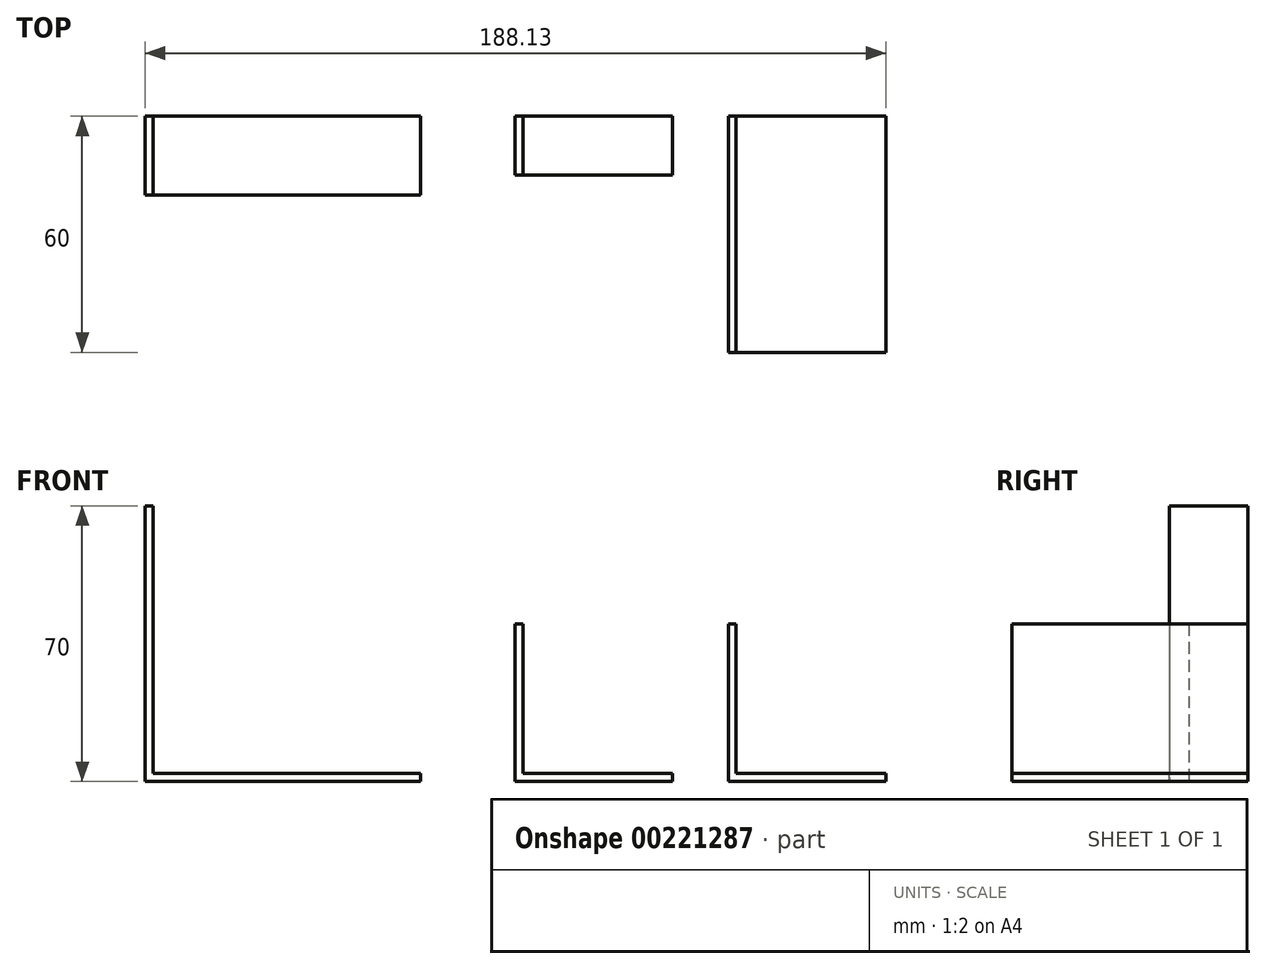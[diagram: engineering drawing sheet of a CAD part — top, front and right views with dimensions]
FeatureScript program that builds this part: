
annotation { "Feature Type Name" : "Feature", "Feature Type Description" : "" }
export const myFeature = defineFeature(function(context is Context, id is Id, definition is map)
    precondition{}
    {
        {
            var Q0;
            Q0=qCreatedBy(makeId("Front.planeOp"),FACE);
            var sketch = newSketch(context, id + "F0", { "sketchPlane" : qUnion([Q0])});
            skLineSegment(sketch, "E0.bottom", {"start": v(-61.82, 70) * mm, "end": v(-59.82, 70) * mm});
            skLineSegment(sketch, "E0.top", {"start": v(-61.82, 0) * mm, "end": v(-59.82, 0) * mm});
            skLineSegment(sketch, "E0.left", {"start": v(-61.82, 70) * mm, "end": v(-61.82, 0) * mm});
            skLineSegment(sketch, "E0.right", {"start": v(-59.82, 70) * mm, "end": v(-59.82, 2) * mm});
            skLineSegment(sketch, "E1.bottom", {"start": v(-61.82, 0) * mm, "end": v(8.18, 0) * mm});
            skLineSegment(sketch, "E1.top", {"start": v(-59.82, 2) * mm, "end": v(8.18, 2) * mm});
            skLineSegment(sketch, "E1.left", {"start": v(-61.82, 0) * mm, "end": v(-61.82, 2) * mm});
            skLineSegment(sketch, "E1.right", {"start": v(8.18, 0) * mm, "end": v(8.18, 2) * mm});
            skLineSegment(sketch, "E2.bottom", {"start": v(32.12, 40) * mm, "end": v(34.12, 40) * mm});
            skLineSegment(sketch, "E2.top", {"start": v(32.12, 0) * mm, "end": v(34.12, 0) * mm});
            skLineSegment(sketch, "E2.left", {"start": v(32.12, 40) * mm, "end": v(32.12, 0) * mm});
            skLineSegment(sketch, "E2.right", {"start": v(34.12, 40) * mm, "end": v(34.12, 2) * mm});
            skLineSegment(sketch, "E3.bottom", {"start": v(34.12, 2) * mm, "end": v(72.12, 2) * mm});
            skLineSegment(sketch, "E3.top", {"start": v(32.12, 0) * mm, "end": v(72.12, 0) * mm});
            skLineSegment(sketch, "E3.left", {"start": v(32.12, 2) * mm, "end": v(32.12, 0) * mm});
            skLineSegment(sketch, "E3.right", {"start": v(72.12, 2) * mm, "end": v(72.12, 0) * mm});
            skLineSegment(sketch, "E4.1.0.0", {"start": v(86.31, 40) * mm, "end": v(86.31, 0) * mm});
            skLineSegment(sketch, "E4.1.0.1", {"start": v(88.31, 40) * mm, "end": v(88.31, 2) * mm});
            skLineSegment(sketch, "E4.1.0.4", {"start": v(86.31, 40) * mm, "end": v(88.31, 40) * mm});
            skLineSegment(sketch, "E4.1.0.6", {"start": v(86.31, 0) * mm, "end": v(88.31, 0) * mm});
            skLineSegment(sketch, "E4.1.0.7", {"start": v(86.31, 2) * mm, "end": v(86.31, 0) * mm});
            skLineSegment(sketch, "E4.direction1", {"start": v(32.12, 0) * mm, "end": v(86.31, 0) * mm, "construction": true});
            skLineSegment(sketch, "E5.bottom", {"start": v(88.31, 2) * mm, "end": v(126.31, 2) * mm});
            skLineSegment(sketch, "E5.right", {"start": v(126.31, 2) * mm, "end": v(126.31, 0) * mm});
            skLineSegment(sketch, "E6.direction1", {"start": v(90.96, -3.8) * mm, "end": v(145.15, -3.8) * mm, "construction": true});
            skLineSegment(sketch, "E7", {"start": v(126.31, 0) * mm, "end": v(86.31, 0) * mm});
            skSolve(sketch);
        }
        {
            var Q0;
            Q0=makeQuery(id+"F0.imprint","IMPRINT",FACE,{"disambiguationData":[TD([[makeQuery(id+"F0.imprint","IMPRINT",EDGE,{"derivedFrom":sQuery(id+"F0.wireOp",EDGE,"E0.bottom")}),-1.0]])]});
            extrude(context, id + "F1", {"entities" : qUnion([Q0]), "depth" : 20 * mm});
        }
        {
            var Q0;
            Q0=makeQuery(id+"F0.imprint","IMPRINT",FACE,{"disambiguationData":[TD([[makeQuery(id+"F0.imprint","IMPRINT",EDGE,{"derivedFrom":sQuery(id+"F0.wireOp",EDGE,"E2.bottom")}),-1.0]])]});
            extrude(context, id + "F2", {"entities" : qUnion([Q0]), "depth" : 15 * mm});
        }
        {
            var Q0;
            Q0=makeQuery(id+"F0.imprint","IMPRINT",FACE,{"disambiguationData":[TD([[makeQuery(id+"F0.imprint","IMPRINT",EDGE,{"derivedFrom":sQuery(id+"F0.wireOp",EDGE,"E4.1.0.0")}),1.0]])]});
            extrude(context, id + "F3", {"entities" : qUnion([Q0]), "depth" : 60 * mm});
        }
    });
